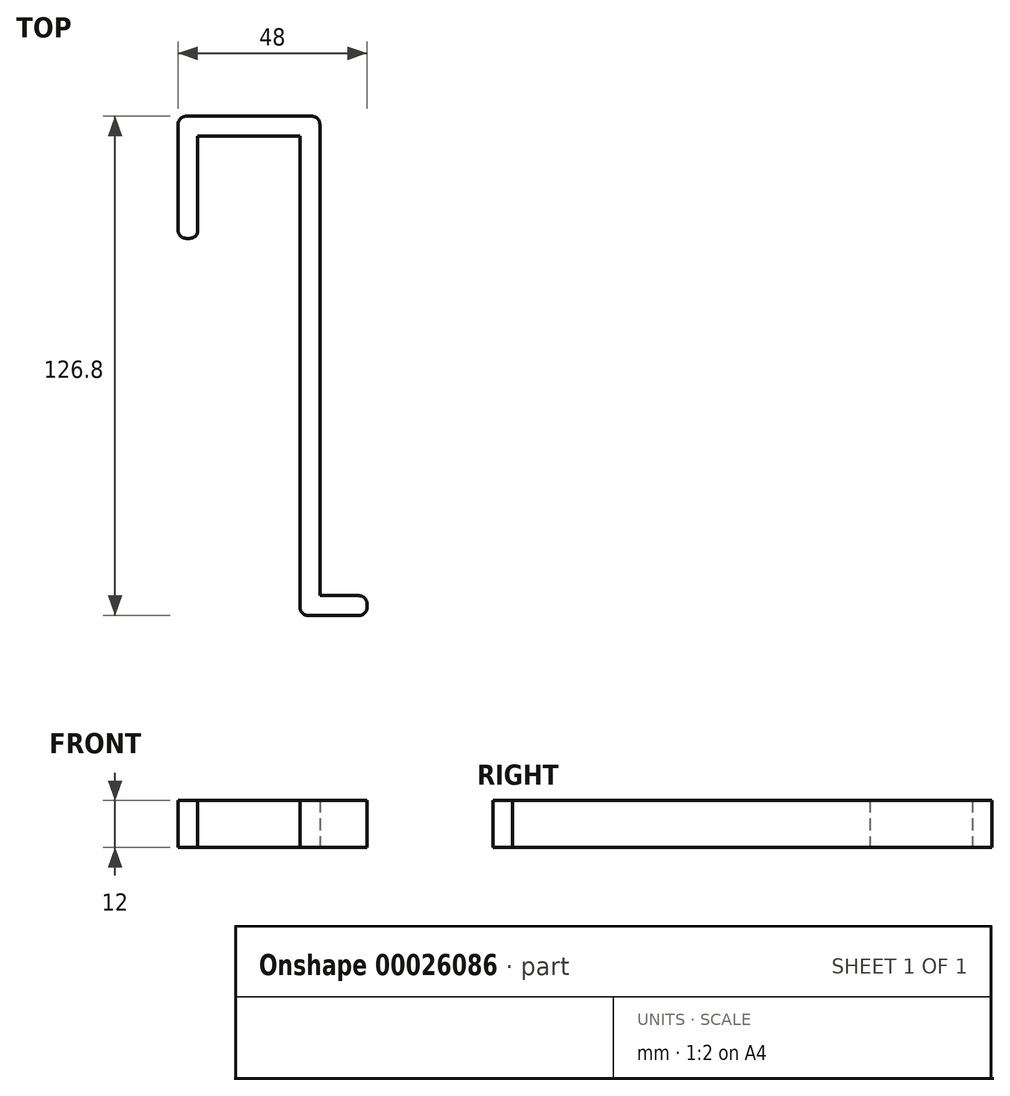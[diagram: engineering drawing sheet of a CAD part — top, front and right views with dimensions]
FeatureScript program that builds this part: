
annotation { "Feature Type Name" : "Feature", "Feature Type Description" : "" }
export const myFeature = defineFeature(function(context is Context, id is Id, definition is map)
    precondition{}
    {
        {
            var Q0;
            Q0=qCreatedBy(makeId("Top.planeOp"),FACE);
            var sketch = newSketch(context, id + "F0", { "sketchPlane" : qUnion([Q0])});
            skLineSegment(sketch, "E0", {"start": v(-26.55, 16.72) * mm, "end": v(-26.55, 40.72) * mm});
            skLineSegment(sketch, "E1", {"start": v(-26.55, 40.72) * mm, "end": v(-0.55, 40.72) * mm});
            skLineSegment(sketch, "E2", {"start": v(-0.55, 40.72) * mm, "end": v(-0.55, -79.08) * mm});
            skLineSegment(sketch, "E3", {"start": v(4.45, -76.08) * mm, "end": v(14.45, -76.08) * mm});
            skLineSegment(sketch, "E4.0", {"start": v(-31.55, 16.72) * mm, "end": v(-31.55, 43.72) * mm});
            skLineSegment(sketch, "E5.0", {"start": v(-29.55, 45.72) * mm, "end": v(2.45, 45.72) * mm});
            skLineSegment(sketch, "E6.0", {"start": v(4.45, 43.72) * mm, "end": v(4.45, -76.08) * mm});
            skLineSegment(sketch, "E7.0", {"start": v(1.45, -81.08) * mm, "end": v(14.45, -81.08) * mm});
            skLineSegment(sketch, "E8", {"start": v(16.45, -78.08) * mm, "end": v(16.45, -79.08) * mm});
            skPoint(sketch, "E9.orphan", {"position": v(-0.55, -76.08) * mm});
            skLineSegment(sketch, "E10", {"start": v(-29.55, 14.72) * mm, "end": v(-28.55, 14.72) * mm});
            skPoint(sketch, "E11.visualSharp", {"position": v(-31.55, 14.72) * mm});
            skArc(sketch, "E11.filletArc", {"start": v(-31.55, 16.72) * mm, "mid": v(-30.96, 15.3) * mm, "end": v(-29.55, 14.72) * mm});
            skPoint(sketch, "E12.visualSharp", {"position": v(-26.55, 14.72) * mm});
            skArc(sketch, "E12.filletArc", {"start": v(-28.55, 14.72) * mm, "mid": v(-27.14, 15.3) * mm, "end": v(-26.55, 16.72) * mm});
            skPoint(sketch, "E13.visualSharp", {"position": v(-31.55, 45.72) * mm});
            skArc(sketch, "E13.filletArc", {"start": v(-29.55, 45.72) * mm, "mid": v(-30.96, 45.13) * mm, "end": v(-31.55, 43.72) * mm});
            skPoint(sketch, "E14.visualSharp", {"position": v(4.45, 45.72) * mm});
            skArc(sketch, "E14.filletArc", {"start": v(4.45, 43.72) * mm, "mid": v(3.86, 45.13) * mm, "end": v(2.45, 45.72) * mm});
            skPoint(sketch, "E15.visualSharp", {"position": v(-0.55, -81.08) * mm});
            skArc(sketch, "E15.filletArc", {"start": v(-0.55, -79.08) * mm, "mid": v(0.04, -80.5) * mm, "end": v(1.45, -81.08) * mm});
            skPoint(sketch, "E16.visualSharp", {"position": v(16.45, -81.08) * mm});
            skArc(sketch, "E16.filletArc", {"start": v(14.45, -81.08) * mm, "mid": v(15.86, -80.5) * mm, "end": v(16.45, -79.08) * mm});
            skPoint(sketch, "E17.visualSharp", {"position": v(16.45, -76.08) * mm});
            skArc(sketch, "E17.filletArc", {"start": v(16.45, -78.08) * mm, "mid": v(15.86, -76.67) * mm, "end": v(14.45, -76.08) * mm});
            skSolve(sketch);
        }
        {
            var Q0;
            Q0=makeQuery(id+"F0.imprint","IMPRINT",FACE,{"disambiguationData":[TD([[makeQuery(id+"F0.imprint","IMPRINT",EDGE,{"derivedFrom":sQuery(id+"F0.wireOp",EDGE,"E0")}),1.0]])]});
            extrude(context, id + "F1", {"entities" : qUnion([Q0]), "depth" : 12 * mm});
        }
    });
